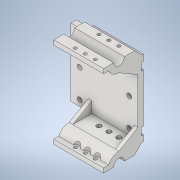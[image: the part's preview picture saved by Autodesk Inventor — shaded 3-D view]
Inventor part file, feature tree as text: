
AUTODESK INVENTOR PART (.ipt)
format: ipt  version: 2020 (Build 240168000, 168)  size: 507,392 bytes
history: native  units: mm
features: extrude x21, sketch x21, pattern_linear x6, other x4, chamfer x4, mirror x2
ambient origin geometry x8: Origin, YZ Plane, XZ Plane, XY Plane, X Axis, Y Axis, Z Axis, Center Point
bodies: Body1 (feature_tree)
feature tree (58):
  other  "Bryła1"
  extrude  "Wyciągnięcie proste1"  Depth=74.0mm
  extrude  "Wyciągnięcie proste2"  Depth=74.0mm
  extrude  "Wyciągnięcie proste3"  Depth=25.0mm TaperAngle=0.0deg
  extrude  "Wyciągnięcie proste4"  Depth=20.0mm
  other  "Płaszczyzna konstrukcyjna1"
  extrude  "Wyciągnięcie proste5"  Depth=20.0mm
  pattern_linear  "Szyk prostokątny1"  Spacing1=11.0mm  [1 undecoded]
  chamfer  "Faza1"  Distance=11.0mm
  chamfer  "Faza2"  Distance=19.8mm
  chamfer  "Faza3"  Distance=2.05mm
  extrude  "Wyciągnięcie proste6"  Depth=7.9mm
  extrude  "Wyciągnięcie proste7"  TaperAngle=0.0deg  [1 undecoded]
  extrude  "Wyciągnięcie proste8"  TaperAngle=0.0deg  [1 undecoded]
  extrude  "Wyciągnięcie proste9"  Depth=2.05mm
  extrude  "Wyciągnięcie proste10"  Depth=7.9mm
  extrude  "Wyciągnięcie proste11"  TaperAngle=0.0deg  [1 undecoded]
  pattern_linear  "Szyk prostokątny2"  Spacing1=0.0mm  [1 undecoded]
  extrude  "Wyciągnięcie proste12"  Depth=1.9mm TaperAngle=0.0deg
  other  "Płaszczyzna konstrukcyjna2"
  mirror  "Odbij1"
  chamfer  "Faza4"  Distance=4.0mm
  extrude  "Wyciągnięcie proste13"  Depth=5.5mm
  pattern_linear  "Szyk prostokątny3"  Spacing1=5.5mm  [1 undecoded]
  extrude  "Wyciągnięcie proste14"  Depth=6.0mm
  pattern_linear  "Szyk prostokątny4"  Spacing1=6.0mm  [1 undecoded]
  extrude  "Wyciągnięcie proste15"  Depth=54.78mm
  pattern_linear  "Szyk prostokątny5"  Spacing1=-37.0mm  [1 undecoded]
  extrude  "Wyciągnięcie proste16"  Depth=27.39mm
  other  "Płaszczyzna konstrukcyjna4"
  mirror  "Odbij3"
  pattern_linear  "Szyk prostokątny6"  Count1=5 Spacing1=0.0mm
  extrude  "Wyciągnięcie proste18"  Depth=30.0mm
  extrude  "Wyciągnięcie proste19"  Depth=2.0mm TaperAngle=45.0deg
  extrude  "Wyciągnięcie proste20"  Depth=3.8999mm TaperAngle=45.0deg
  extrude  "Wyciągnięcie proste21"  Depth=3.8999mm TaperAngle=45.0deg
  extrude  "Wyciągnięcie proste22"  Depth=22.9mm TaperAngle=0.0deg
  sketch  "Szkic1"
  sketch  "Szkic2"
  sketch  "Szkic3"
  sketch  "Szkic4"
  sketch  "Szkic5"
  sketch  "Szkic6"
  sketch  "Szkic7"
  sketch  "Szkic8"
  sketch  "Szkic9"
  sketch  "Szkic10"
  sketch  "Szkic12"
  sketch  "Szkic13"
  sketch  "Szkic15"
  sketch  "Szkic16"
  sketch  "Szkic17"
  sketch  "Szkic18"
  sketch  "Szkic20"
  sketch  "Szkic21"
  sketch  "Szkic22"
  sketch  "Szkic23"
  sketch  "Szkic24"
note: 8 required parameter values undecoded (feature->parameter linkage not recoverable at this tier; creation-order binding heuristic only, values carry confidence <= 0.55)
